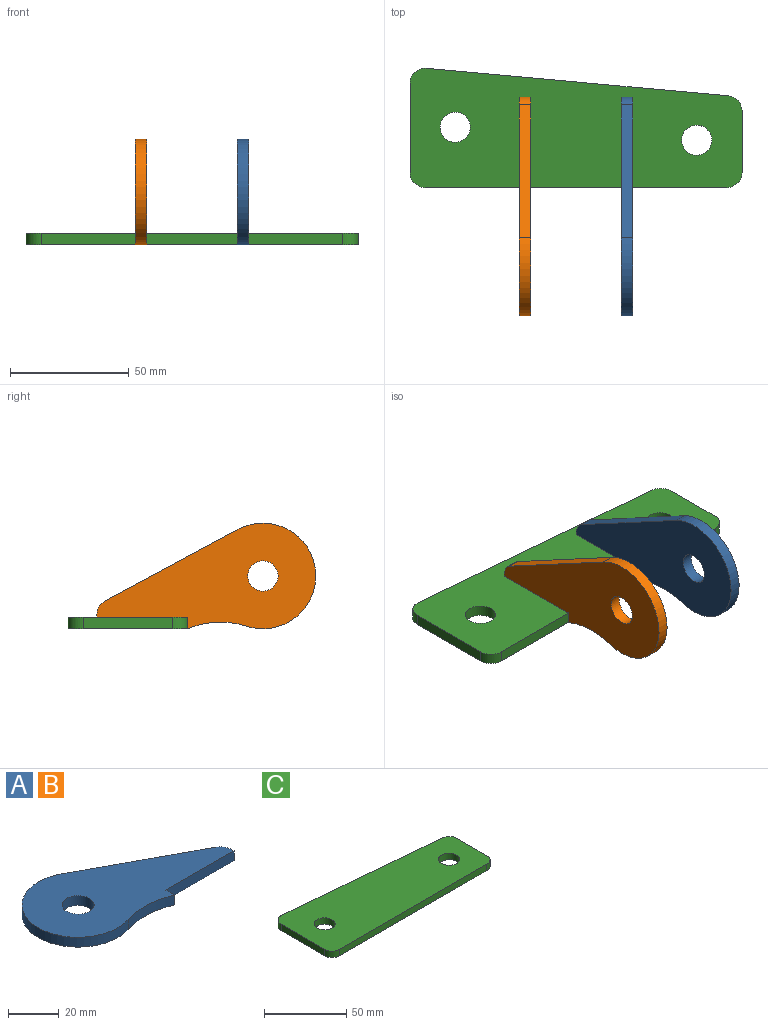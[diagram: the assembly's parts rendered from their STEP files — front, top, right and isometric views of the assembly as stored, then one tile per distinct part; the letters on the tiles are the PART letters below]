
ASSEMBLY  parts=3 mates=2
PART A: 10 faces, bbox 92.1x44.5x4.8 mm
  f0: plane 38.1x4.76mm, normal (0,-1,0), area 181.5mm2, adj f1,f7,f8,f9
  f1: plane 4.76x1.26mm, normal (1,0,0), area 6mm2, adj f0,f2,f8,f9
  f2: cylinder r=6.35mm len=5.59mm, axis (0,0,-1), area 32.5mm2, adj f1,f3,f8,f9
  f3: plane 55.97x30.18mm, normal (0.47,0.88,0), area 302.8mm2, adj f2,f4,f8,f9
  f4: cylinder r=22.23mm len=44.45mm, axis (0,0,-1), area 418mm2, adj f3,f5,f8,f9
  f5: cylinder r=35.7mm len=24.91mm, axis (0,0,-1), area 121.3mm2, adj f4,f7,f8,f9
  f6: cylinder r=6.35mm len=12.7mm, axis (0,0,-1), area 190mm2, adj f8,f9
  f7: plane 4.78x4.76mm, normal (1,0,0), area 22.7mm2, adj f0,f5,f8,f9
  f8: plane 92.08x44.46mm, normal (0,0,1), area 2401.8mm2, adj f0,f1,f2,f3,f4,f5,f6,f7
  f9: plane 92.08x44.46mm, normal (0,0,-1), area 2401.8mm2, adj f0,f1,f2,f3,f4,f5,f6,f7
PART B: same geometry as A
PART C: 12 faces, bbox 139.7x50.2x4.8 mm
  f0: plane 37.5x4.76mm, normal (-1,0,0), area 178.6mm2, adj f1,f9,f10,f11
  f1: cylinder r=6.35mm len=6.35mm, axis (0,0,-1), area 47.5mm2, adj f0,f2,f10,f11
  f2: plane 127x4.76mm, normal (0,-1,0), area 604.8mm2, adj f1,f3,f10,f11
  f3: cylinder r=6.35mm len=6.35mm, axis (0,0,-1), area 47.5mm2, adj f2,f4,f10,f11
  f4: plane 25.95x4.76mm, normal (1,0,0), area 123.6mm2, adj f3,f5,f10,f11
  f5: cylinder r=6.35mm len=6.32mm, axis (0,0,-1), area 44.8mm2, adj f4,f6,f10,f11
  f6: plane 127x11.55mm, normal (0.09,1,0), area 607.3mm2, adj f5,f9,f10,f11
  f7: cylinder r=6.35mm len=12.7mm, axis (0,0,-1), area 190mm2, adj f10,f11
  f8: cylinder r=6.35mm len=12.7mm, axis (0,0,-1), area 190.1mm2, adj f10,f11
  f9: cylinder r=6.35mm len=6.93mm, axis (0,0,-1), area 50.2mm2, adj f0,f6,f10,f11
  f10: plane 139.7x50.2mm, normal (0,0,1), area 5921.3mm2, adj f0,f1,f2,f3,f4,f5,f6,f7
  f11: plane 139.7x50.2mm, normal (0,0,-1), area 5921.3mm2, adj f0,f1,f2,f3,f4,f5,f6,f7
PLACE A rot(axis=(0.58,0.58,0.58),120deg) t=(12.05,123.38,71.47)mm
PLACE B rot(axis=(0.58,0.58,0.58),120deg) t=(-30.81,123.38,71.47)mm
PLACE C t=(-22.93,-14.08,12.65)mm
MATE fastened B.f0 <-> C.f10  axis (0,0,-1) through (-28.43,-19.12,17.41)mm
MATE fastened A.f4 <-> B.f4  axis (-1,0,0) through (12.05,-50.87,34.87)mm
